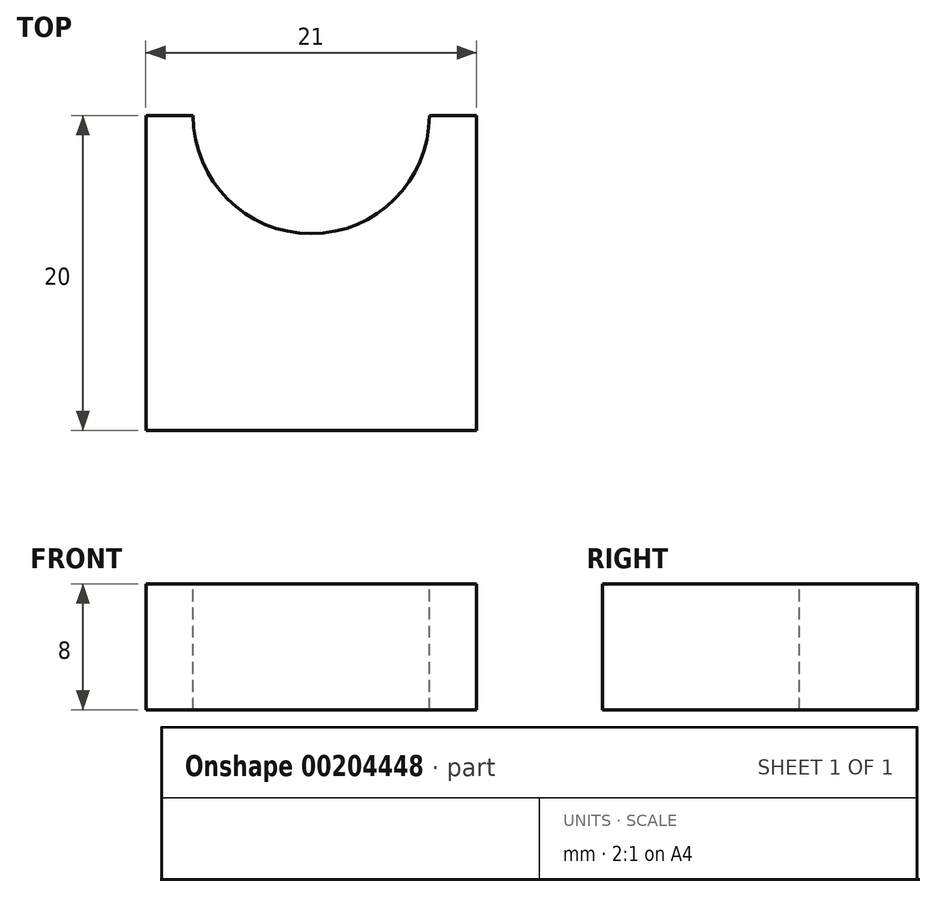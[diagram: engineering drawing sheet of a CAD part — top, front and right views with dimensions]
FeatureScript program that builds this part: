
annotation { "Feature Type Name" : "Feature", "Feature Type Description" : "" }
export const myFeature = defineFeature(function(context is Context, id is Id, definition is map)
    precondition{}
    {
        {
            var Q0;
            Q0=qCreatedBy(makeId("Top.planeOp"),FACE);
            var sketch = newSketch(context, id + "F0", { "sketchPlane" : qUnion([Q0])});
            skLineSegment(sketch, "E0", {"start": v(-15.8, 20) * mm, "end": v(5.2, 20) * mm});
            skLineSegment(sketch, "E1", {"start": v(-15.8, 20) * mm, "end": v(-15.8, 0) * mm});
            skLineSegment(sketch, "E2", {"start": v(5.2, 20) * mm, "end": v(5.2, 0) * mm});
            skLineSegment(sketch, "E3", {"start": v(5.2, 0) * mm, "end": v(-15.8, 0) * mm});
            skSolve(sketch);
        }
        {
            var Q0;
            Q0 = qSketchRegion(id + "F0", true);
            extrude(context, id + "F1", {"entities" : qUnion([Q0]), "endBound" : BoundingType.SYMMETRIC, "depth" : 8 * mm});
        }
        {
            var Q0;
            Q0=makeQuery(id+"F1.opExtrude","CAP_FACE",FACE,{"disambiguationData":[OSD([sQuery(id+"F0.wireOp",EDGE,"E0"),sQuery(id+"F0.wireOp",EDGE,"E1"),sQuery(id+"F0.wireOp",EDGE,"E2"),sQuery(id+"F0.wireOp",EDGE,"E3")])],"isStart":false});
            var sketch = newSketch(context, id + "F2", { "sketchPlane" : qUnion([Q0])});
            skPoint(sketch, "E4", {"position": v(-5.3, 20) * mm});
            skSolve(sketch);
        }
        {
            var Q0;
            Q0=sQuery(id+"F2.wireOp",VERTEX,"E4");
            var Q1;
            Q1=makeQuery(id+"F1.opExtrude","SWEPT_BODY",BODY,{"disambiguationData":[OSD([sQuery(id+"F0.wireOp",EDGE,"E0"),sQuery(id+"F0.wireOp",EDGE,"E1"),sQuery(id+"F0.wireOp",EDGE,"E2"),sQuery(id+"F0.wireOp",EDGE,"E3")])]});
            hole(context, id + "F3", {"style" : HoleStyle.SIMPLE, "endStyle" : HoleEndStyle.THROUGH, "holeDiameter" : 15 * mm, "locations" : qUnion([Q0]), "scope" : qUnion([Q1]), "isTappedThrough" : true});
        }
    });
